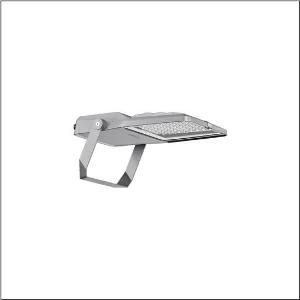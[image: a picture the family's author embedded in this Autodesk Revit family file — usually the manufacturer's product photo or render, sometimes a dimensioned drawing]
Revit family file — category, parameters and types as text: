
# Revit family: floodlight_fl_21_iq_mini___pl43_5xa7771b2a1a_26ba
name_source: partatom
category: Lighting Fixtures
units: mm (PartAtom-declared; Revit-internal decimal feet)

## family parameters
Cut with Voids When Loaded = No
Host = Face
Light Source = No
Part Type = Normal
Room Calculation Point = No
Round Connector Dimension = Use Diameter
Shared = No

## types (1)
- --- (1 x LED, 6400 lm, 45.5 W, 3000K)
    Apparent Load = 46 VA
    CIE Flux Codes = 27 78 99 100 100
    Color Rendering = 70
    Color Temperature = 3000K
    Default Elevation = 1800 mm
    Description = Floodlight FL 21 iQ mini, floodlight, primary light control with lens, of PMMA, primary optical cover: protective disc, of toughened safety glass, transparent, light distribution: PL43, light emission: direct distribution, installation type: surface-mounted, LED, High Power LED, rated luminous flux: 6.400lm, luminous efficacy: 141lm/W, light colour: 730, colour temperature: 3000K, control: Auto-Match, Temp-Guard, Lumen-Switch, Night-Set, Smart-Wire, Light-Fading, Desk-Remote (wireless, voltage-free reading and setting of iQ features in the workshop via application-optimized NFC function/RFID function), optimised constant luminous flux control (CLO 2.0), with terminal, 6-pole, mains connection: 220..240V, AC, 50/60Hz, start of lifetime: 46W, end of service life: 48W, reduction: 22W, luminaire housing, of diecast aluminium, powder-coated, Siteco® metallic grey (DB 702S), corrosivity category C5 mid according to DIN EN ISO 12944, sealing non-destructively replaceable, mounting bracket, of steel, galvanised, powder-coated, Siteco® metallic grey (DB 702S), protection rating (complete): IP66, insulation class (complete): insulation class II (safety insulation), certification: CE, ENEC, VDE, protection symbol: D, impact resistance: IK08, permissible operating ambient temperature: -40..+40°C, permissible operating ambient temperature for outdoor applications: -40..+50°C, standard: DIN EN 12944, LABS conformity tested according to VDMA 24364:2018-05, packaging unit: 1 piece

Light Distribution: PL43
    Height = 70 mm
    Lamp = 1 x LED
    Lamp Light Flux = 6400 lm
    Lamp Power = 45.5 W
    Lamp count = 1
    Length = 485 mm
    Luminous efficacy = 141 lm/W
    Manufacturer = Siteco
    ModVariant = No
    Model = 5XA7771B2A1A
    Mounting Place = Wall
    Mounting Type = Surface mounted
    Number of Poles = 1
    OnlyDefault = Yes
    Power Factor = 1
    Product Name = Floodlight FL 21 iQ mini | PL43
    Product group = floodlight | wall mounted
    ProductGroupID = 2001
    Protection Class = Protection class II
    Protection Degree = IP 66
    RLX_Detail_Level = 1
    RLX_Emergency_Light_Flux = 0 lm
    RLX_Emergency_Type = 0
    RLX_Emergency_Type_DB = No
    RlxData = <blob elided: 96029 chars, md5=47122537>
    Socket = socket
    Standby Power = 0 W
    System Light Flux = 6400 lm
    System Power = 46 W
    Type Comments = factory setting: luminous flux: 100 % | dim-lin: 254 | 463 mA
    Type Image = l_1006845.jpg
    URL = http://relux.com
    VarID = @adj_095377
    Voltage = 0 V
    Weight = 0.00 kg
    Width = 337 mm

## geometry (parser evidence)
native form markers: Blend x4, Sweep x13
no freeform markers — native parametric forms only
